annotation { "Feature Type Name" : "Feature", "Feature Type Description" : "" }
export const myFeature = defineFeature(function(context is Context, id is Id, definition is map)
    precondition{}
    {
        {
            var Q0;
            Q0=qCreatedBy(makeId("Front.planeOp"),FACE);
            var sketch = newSketch(context, id + "F0", { "sketchPlane" : qUnion([Q0])});
            skLineSegment(sketch, "E0", {"start": v(0, 0) * mm, "end": v(-4572, 0) * mm});
            skLineSegment(sketch, "E1", {"start": v(0, 0) * mm, "end": v(4572, 0) * mm});
            skLineSegment(sketch, "E2", {"start": v(0, 0) * mm, "end": v(0, 3048) * mm});
            skLineSegment(sketch, "E3", {"start": v(0, 3048) * mm, "end": v(-4572, 0) * mm});
            skLineSegment(sketch, "E4", {"start": v(4572, 0) * mm, "end": v(0, 3048) * mm});
            skLineSegment(sketch, "E5", {"start": v(-4572, 0) * mm, "end": v(-5486.4, 0) * mm});
            skLineSegment(sketch, "E6", {"start": v(0, 3048) * mm, "end": v(0, 3505.2) * mm});
            skLineSegment(sketch, "E7", {"start": v(-5486.4, 0) * mm, "end": v(0, 3505.2) * mm});
            skLineSegment(sketch, "E8.left", {"start": v(4572, 0) * mm, "end": v(4572, 0) * mm});
            skLineSegment(sketch, "E9", {"start": v(4572, 0) * mm, "end": v(5486.4, 0) * mm});
            skLineSegment(sketch, "E10", {"start": v(5486.4, 0) * mm, "end": v(0, 3505.2) * mm});
            skLineSegment(sketch, "E11", {"start": v(-4572, 0) * mm, "end": v(-4572, -4267.2) * mm});
            skLineSegment(sketch, "E12", {"start": v(4572, 0) * mm, "end": v(4572, -4267.2) * mm});
            skLineSegment(sketch, "E13", {"start": v(4572, -4267.2) * mm, "end": v(-4572, -4267.2) * mm});
            skLineSegment(sketch, "E14", {"start": v(-4572, -4267.2) * mm, "end": v(-4572, -4876.8) * mm});
            skLineSegment(sketch, "E15", {"start": v(4572, -4267.2) * mm, "end": v(4572, -4876.8) * mm});
            skLineSegment(sketch, "E16", {"start": v(4572, -4876.8) * mm, "end": v(-4572, -4876.8) * mm});
            skLineSegment(sketch, "E17", {"start": v(4572, -4876.8) * mm, "end": v(9144, -4876.8) * mm});
            skLineSegment(sketch, "E18", {"start": v(4572, -4267.2) * mm, "end": v(9144, -4267.2) * mm});
            skLineSegment(sketch, "E19", {"start": v(9144, -4267.2) * mm, "end": v(9144, -4876.8) * mm});
            skLineSegment(sketch, "E20", {"start": v(9144, -4267.2) * mm, "end": v(9144, -609.6) * mm});
            skLineSegment(sketch, "E21", {"start": v(9144, -609.6) * mm, "end": v(4572, 0) * mm});
            skLineSegment(sketch, "E22", {"start": v(4572, -609.6) * mm, "end": v(9144, -609.6) * mm});
            skLineSegment(sketch, "E23.bottom", {"start": v(1524, -1219.2) * mm, "end": v(3352.8, -1219.2) * mm});
            skLineSegment(sketch, "E23.top", {"start": v(1524, -2438.4) * mm, "end": v(3352.8, -2438.4) * mm});
            skLineSegment(sketch, "E23.left", {"start": v(1524, -1219.2) * mm, "end": v(1524, -2438.4) * mm});
            skLineSegment(sketch, "E23.right", {"start": v(3352.8, -1219.2) * mm, "end": v(3352.8, -2438.4) * mm});
            skLineSegment(sketch, "E24.0", {"start": v(1219.2, -914.4) * mm, "end": v(3657.6, -914.4) * mm});
            skLineSegment(sketch, "E24.1", {"start": v(1219.2, -914.4) * mm, "end": v(1219.2, -2743.2) * mm});
            skLineSegment(sketch, "E24.2", {"start": v(1219.2, -2743.2) * mm, "end": v(3657.6, -2743.2) * mm});
            skLineSegment(sketch, "E24.3", {"start": v(3657.6, -914.4) * mm, "end": v(3657.6, -2743.2) * mm});
            skLineSegment(sketch, "E25", {"start": v(-3324.84, -4267.2) * mm, "end": v(-3352.8, -2133.78) * mm});
            skLineSegment(sketch, "E26", {"start": v(-2105.64, -4267.2) * mm, "end": v(-2105.64, -2133.6) * mm});
            skLineSegment(sketch, "E27", {"start": v(-3352.8, -2133.78) * mm, "end": v(-2105.64, -2133.6) * mm});
            skLineSegment(sketch, "E28", {"start": v(-2105.64, -4267.2) * mm, "end": v(-3324.84, -4267.2) * mm});
            skLineSegment(sketch, "E29.bottom", {"start": v(5791.2, -1828.8) * mm, "end": v(7924.8, -1828.8) * mm});
            skLineSegment(sketch, "E29.top", {"start": v(5791.2, -3352.8) * mm, "end": v(7924.8, -3352.8) * mm});
            skLineSegment(sketch, "E29.left", {"start": v(5791.2, -1828.8) * mm, "end": v(5791.2, -3352.8) * mm});
            skLineSegment(sketch, "E29.right", {"start": v(7924.8, -1828.8) * mm, "end": v(7924.8, -3352.8) * mm});
            skLineSegment(sketch, "E30.0", {"start": v(5516.88, -1554.48) * mm, "end": v(8199.12, -1554.48) * mm});
            skLineSegment(sketch, "E30.1", {"start": v(5516.88, -1554.48) * mm, "end": v(5516.88, -3627.12) * mm});
            skLineSegment(sketch, "E30.2", {"start": v(5516.88, -3627.12) * mm, "end": v(8199.12, -3627.12) * mm});
            skLineSegment(sketch, "E30.3", {"start": v(8199.12, -1554.48) * mm, "end": v(8199.12, -3627.12) * mm});
            skLineSegment(sketch, "E31.0", {"start": v(-4577, 0) * mm, "end": v(-4577, -4267.2) * mm});
            skSolve(sketch);
        }
        {
            var Q0;
            {var subQ3=sQuery(id+"F0.wireOp",EDGE,"E3");Q0=makeQuery(id+"F0.imprint","IMPRINT",FACE,{"disambiguationData":[TD([[makeQuery(id+"F0.imprint","IMPRINT",EDGE,{"derivedFrom":subQ3}),-1.0]])]});}
            var Q1;
            Q1=makeQuery(id+"F0.imprint","IMPRINT",FACE,{"disambiguationData":[TD([[makeQuery(id+"F0.imprint","IMPRINT",EDGE,{"derivedFrom":sQuery(id+"F0.wireOp",EDGE,"E4")}),-1.0]])]});
            extrude(context, id + "F1", {"entities" : qUnion([Q0, Q1]), "endBound" : BoundingType.SYMMETRIC, "depth" : 14020.8 * mm, "offsetDistance" : 30.48 * mm});
        }
        {
            var Q0;
            {var subQ0=sQuery(id+"F0.wireOp",EDGE,"E21");Q0=makeQuery(id+"F0.imprint","IMPRINT",FACE,{"disambiguationData":[TD([[makeQuery(id+"F0.imprint","IMPRINT",EDGE,{"derivedFrom":subQ0}),1.0]])]});}
            extrude(context, id + "F2", {"entities" : qUnion([Q0]), "endBound" : BoundingType.SYMMETRIC, "depth" : 14020.8 * mm, "offsetDistance" : 30.48 * mm});
        }
        {
            var Q0;
            Q0=makeQuery(id+"F0.imprint","IMPRINT",FACE,{"disambiguationData":[TD([[makeQuery(id+"F0.imprint","IMPRINT",EDGE,{"derivedFrom":sQuery(id+"F0.wireOp",EDGE,"E0")}),-1.0]])]});
            var Q1;
            Q1=makeQuery(id+"F0.imprint","IMPRINT",FACE,{"disambiguationData":[TD([[makeQuery(id+"F0.imprint","IMPRINT",EDGE,{"derivedFrom":sQuery(id+"F0.wireOp",EDGE,"E1")}),1.0]])]});
            var Q2;
            Q2=makeQuery(id+"F0.imprint","IMPRINT",FACE,{"disambiguationData":[TD([[makeQuery(id+"F0.imprint","IMPRINT",EDGE,{"derivedFrom":sQuery(id+"F0.wireOp",EDGE,"E0")}),1.0]])]});
            var Q3;
            {var subQ1=sQuery(id+"F0.wireOp",EDGE,"E18");Q3=makeQuery(id+"F0.imprint","IMPRINT",FACE,{"disambiguationData":[TD([[makeQuery(id+"F0.imprint","IMPRINT",EDGE,{"derivedFrom":subQ1}),1.0]])]});}
            extrude(context, id + "F3", {"entities" : qUnion([Q0, Q1, Q2, Q3]), "endBound" : BoundingType.SYMMETRIC, "depth" : 13106.4 * mm, "offsetDistance" : 30.48 * mm});
        }
        {
            var Q0;
            Q0=makeQuery(id+"F0.imprint","IMPRINT",FACE,{"disambiguationData":[TD([[makeQuery(id+"F0.imprint","IMPRINT",EDGE,{"derivedFrom":sQuery(id+"F0.wireOp",EDGE,"E25")}),-1.0]])]});
            extrude(context, id + "F4", {"entities" : qUnion([Q0]), "operationType" : NewBodyOperationType.ADD, "endBound" : BoundingType.SYMMETRIC, "depth" : 13106.4 * mm, "offsetDistance" : 30.48 * mm});
        }
        {
            var Q0;
            Q0=makeQuery(id+"F0.imprint","IMPRINT",FACE,{"disambiguationData":[TD([[makeQuery(id+"F0.imprint","IMPRINT",EDGE,{"derivedFrom":sQuery(id+"F0.wireOp",EDGE,"E29.bottom")}),1.0]])]});
            var Q1;
            Q1=makeQuery(id+"F0.imprint","IMPRINT",FACE,{"disambiguationData":[TD([[makeQuery(id+"F0.imprint","IMPRINT",EDGE,{"derivedFrom":sQuery(id+"F0.wireOp",EDGE,"E23.bottom")}),1.0]])]});
            extrude(context, id + "F5", {"entities" : qUnion([Q0, Q1]), "operationType" : NewBodyOperationType.ADD, "endBound" : BoundingType.SYMMETRIC, "depth" : 13411.2 * mm, "offsetDistance" : 30.48 * mm});
        }
        {
            var Q0;
            Q0=makeQuery(id+"F0.imprint","IMPRINT",FACE,{"disambiguationData":[TD([[makeQuery(id+"F0.imprint","IMPRINT",EDGE,{"derivedFrom":sQuery(id+"F0.wireOp",EDGE,"E23.bottom")}),-1.0]])]});
            var Q1;
            Q1=makeQuery(id+"F0.imprint","IMPRINT",FACE,{"disambiguationData":[TD([[makeQuery(id+"F0.imprint","IMPRINT",EDGE,{"derivedFrom":sQuery(id+"F0.wireOp",EDGE,"E29.bottom")}),-1.0]])]});
            extrude(context, id + "F6", {"entities" : qUnion([Q0, Q1]), "operationType" : NewBodyOperationType.ADD, "endBound" : BoundingType.SYMMETRIC, "depth" : 13106.4 * mm, "offsetDistance" : 30.48 * mm});
        }
        {
            var Q0;
            {var subQ1=sQuery(id+"F0.wireOp",EDGE,"E14");Q0=makeQuery(id+"F0.imprint","IMPRINT",FACE,{"disambiguationData":[TD([[makeQuery(id+"F0.imprint","IMPRINT",EDGE,{"derivedFrom":subQ1}),1.0]])]});}
            var Q1;
            Q1=makeQuery(id+"F0.imprint","IMPRINT",FACE,{"disambiguationData":[TD([[makeQuery(id+"F0.imprint","IMPRINT",EDGE,{"derivedFrom":sQuery(id+"F0.wireOp",EDGE,"E15")}),1.0]])]});
            extrude(context, id + "F7", {"entities" : qUnion([Q0, Q1]), "operationType" : NewBodyOperationType.ADD, "endBound" : BoundingType.SYMMETRIC, "depth" : 13716 * mm, "offsetDistance" : 30.48 * mm});
        }
        {
            var Q0;
            Q0=qCreatedBy(makeId("Front.planeOp"),FACE);
            var sketch = newSketch(context, id + "F8", { "sketchPlane" : qUnion([Q0])});
            skText(sketch, "E32", { "text": "Trevor Cox", "fontName": "OpenSans-Bold.ttf"});
            const initialGuessF8  = {"E32": [-3.383, -6.30916, 1, 0, 1.10805]};
            skSetInitialGuess(sketch, initialGuessF8);
            skSolve(sketch);
        }
        {
            var Q0;
            Q0 = qSketchRegion(id + "F8", true);
            extrude(context, id + "F9", {"entities" : qUnion([Q0]), "depth" : 853.44 * mm, "offsetDistance" : 30.48 * mm});
        }
    });